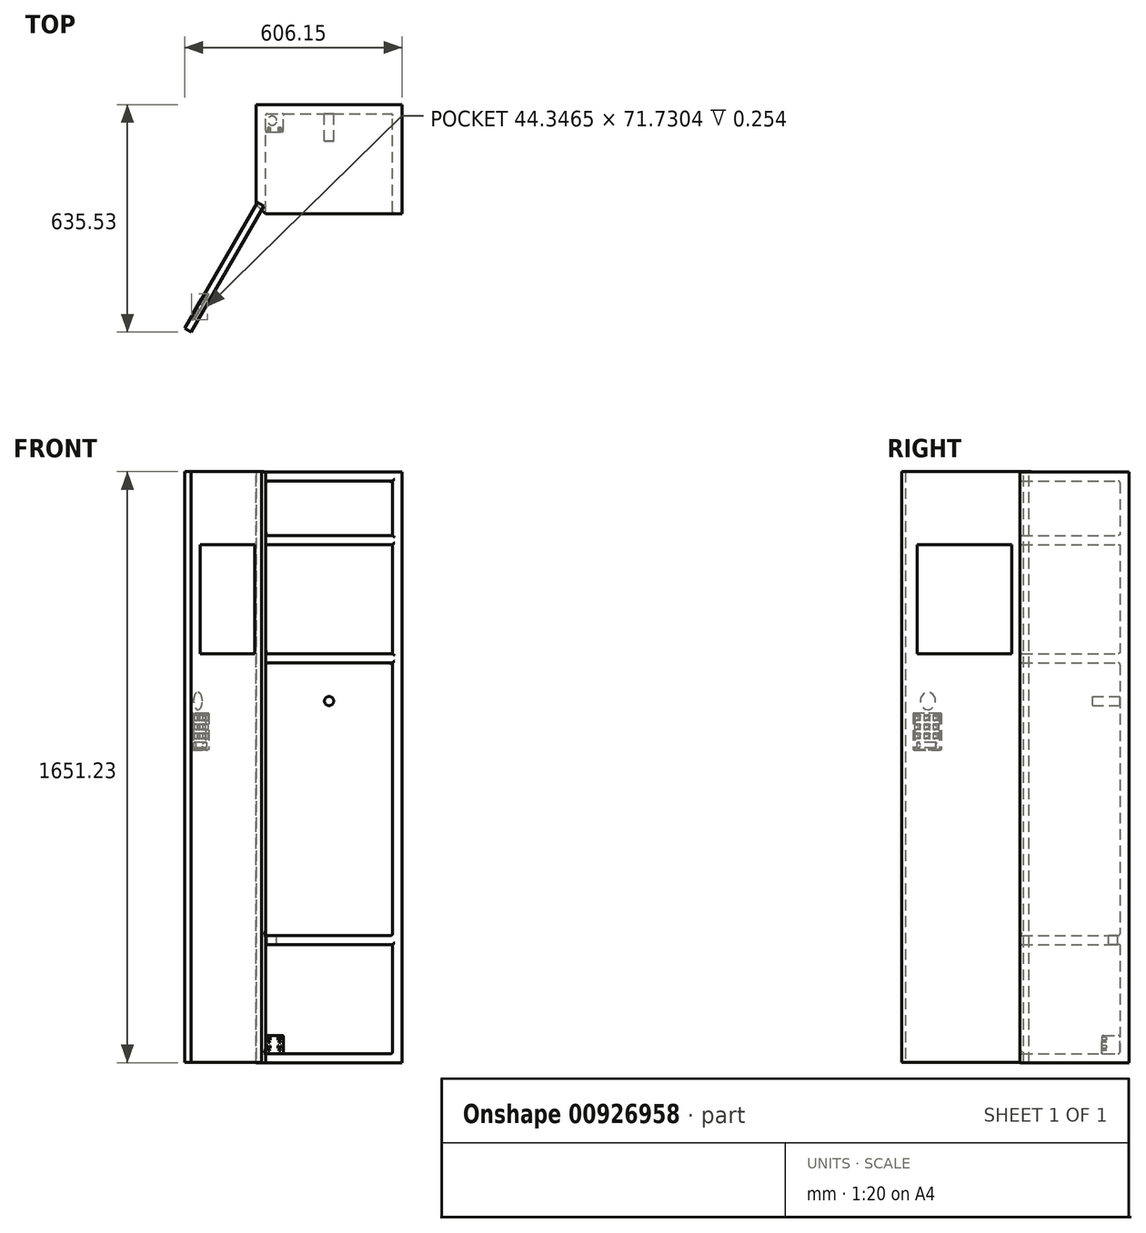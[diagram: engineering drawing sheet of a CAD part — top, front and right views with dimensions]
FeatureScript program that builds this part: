
annotation { "Feature Type Name" : "Feature", "Feature Type Description" : "" }
export const myFeature = defineFeature(function(context is Context, id is Id, definition is map)
    precondition{}
    {
        {
            var Q0;
            Q0=qCreatedBy(makeId("Front.planeOp"),FACE);
            var sketch = newSketch(context, id + "F0", { "sketchPlane" : qUnion([Q0])});
            skLineSegment(sketch, "E0.bottom", {"start": v(-230.27, 1365.34) * mm, "end": v(176.13, 1365.34) * mm});
            skLineSegment(sketch, "E0.top", {"start": v(-230.27, -285.66) * mm, "end": v(176.13, -285.66) * mm});
            skLineSegment(sketch, "E0.left", {"start": v(-230.27, 1365.34) * mm, "end": v(-230.27, -285.66) * mm});
            skLineSegment(sketch, "E0.right", {"start": v(176.13, 1365.34) * mm, "end": v(176.13, -285.66) * mm});
            skSolve(sketch);
        }
        {
            var Q0;
            Q0 = qSketchRegion(id + "F0", true);
            extrude(context, id + "F1", {"entities" : qUnion([Q0]), "depth" : 304.8 * mm, "offsetDistance" : 25.4 * mm});
        }
        {
            var Q0;
            Q0=makeQuery(id+"F1.opExtrude","CAP_FACE",FACE,{"disambiguationData":[OSD([sQuery(id+"F0.wireOp",EDGE,"E0.bottom"),sQuery(id+"F0.wireOp",EDGE,"E0.top"),sQuery(id+"F0.wireOp",EDGE,"E0.left"),sQuery(id+"F0.wireOp",EDGE,"E0.right")])],"isStart":false});
            shell(context, id + "F2", {"entities" : qUnion([Q0]), "thickness" : 25.4 * mm});
        }
        {
            var Q0;
            Q0=makeQuery(id+"F2.opShell","OFFSET_FACE",FACE,{"disambiguationData":[OSD([sQuery(id+"F0.wireOp",EDGE,"E0.bottom"),sQuery(id+"F0.wireOp",EDGE,"E0.top"),sQuery(id+"F0.wireOp",EDGE,"E0.left"),sQuery(id+"F0.wireOp",EDGE,"E0.right")])]});
            var sketch = newSketch(context, id + "F3", { "sketchPlane" : qUnion([Q0])});
            skLineSegment(sketch, "E1.bottom", {"start": v(-204.87, 1187.54) * mm, "end": v(150.73, 1187.54) * mm});
            skLineSegment(sketch, "E1.top", {"start": v(-204.87, 1162.14) * mm, "end": v(150.73, 1162.14) * mm});
            skLineSegment(sketch, "E1.left", {"start": v(-204.87, 1187.54) * mm, "end": v(-204.87, 1162.14) * mm});
            skLineSegment(sketch, "E1.right", {"start": v(150.73, 1187.54) * mm, "end": v(150.73, 1162.14) * mm});
            skSolve(sketch);
        }
        {
            var Q0;
            Q0 = qSketchRegion(id + "F3", true);
            extrude(context, id + "F4", {"entities" : qUnion([Q0]), "operationType" : NewBodyOperationType.ADD, "depth" : 279.4 * mm, "offsetDistance" : 25.4 * mm});
        }
        {
            var Q0;
            {var subQ0=sQuery(id+"F0.wireOp",EDGE,"E0.top");var subQ1=sQuery(id+"F0.wireOp",EDGE,"E0.left");var subQ2=sQuery(id+"F0.wireOp",EDGE,"E0.right");Q0=makeQuery(id+"F4.boolean.opBoolean","SPLIT",FACE,{"disambiguationData":[TD([makeQuery(id+"F2.opShell","OFFSET_FACE",FACE,{"disambiguationData":[OSD([subQ0])]})])],"derivedFrom":makeQuery(id+"F2.opShell","OFFSET_FACE",FACE,{"disambiguationData":[OSD([sQuery(id+"F0.wireOp",EDGE,"E0.bottom"),subQ0,subQ1,subQ2])]})});}
            var sketch = newSketch(context, id + "F5", { "sketchPlane" : qUnion([Q0])});
            skLineSegment(sketch, "E2.bottom", {"start": v(-204.87, 857.34) * mm, "end": v(150.73, 857.34) * mm});
            skLineSegment(sketch, "E2.top", {"start": v(-204.87, 831.94) * mm, "end": v(150.73, 831.94) * mm});
            skLineSegment(sketch, "E2.left", {"start": v(-204.87, 857.34) * mm, "end": v(-204.87, 831.94) * mm});
            skLineSegment(sketch, "E2.right", {"start": v(150.73, 857.34) * mm, "end": v(150.73, 831.94) * mm});
            skLineSegment(sketch, "E3.bottom", {"start": v(-204.87, 44.54) * mm, "end": v(150.73, 44.54) * mm});
            skLineSegment(sketch, "E3.top", {"start": v(-204.87, 69.94) * mm, "end": v(150.73, 69.94) * mm});
            skLineSegment(sketch, "E3.left", {"start": v(-204.87, 44.54) * mm, "end": v(-204.87, 69.94) * mm});
            skLineSegment(sketch, "E3.right", {"start": v(150.73, 44.54) * mm, "end": v(150.73, 69.94) * mm});
            skSolve(sketch);
        }
        {
            var Q0;
            Q0 = qSketchRegion(id + "F5", true);
            extrude(context, id + "F6", {"entities" : qUnion([Q0]), "operationType" : NewBodyOperationType.ADD, "depth" : 279.4 * mm, "offsetDistance" : 25.4 * mm});
        }
        {
            var Q0;
            Q0 = qSketchRegion(id + "F5", true);
            extrude(context, id + "F7", {"entities" : qUnion([Q0]), "operationType" : NewBodyOperationType.ADD, "depth" : 25.4 * mm, "offsetDistance" : 25.4 * mm});
        }
        {
            var Q0;
            {var subQ0=sQuery(id+"F0.wireOp",EDGE,"E0.left");var subQ2=sQuery(id+"F0.wireOp",EDGE,"E0.right");var subQ4=sQuery(id+"F0.wireOp",EDGE,"E0.top");Q0=makeQuery(id+"F6.boolean.opBoolean","SPLIT",FACE,{"disambiguationData":[TD([makeQuery(id+"F6.opExtrude","SWEPT_FACE",FACE,{"disambiguationData":[OSD([sQuery(id+"F5.wireOp",EDGE,"E2.top")])]})])],"derivedFrom":makeQuery(id+"F4.boolean.opBoolean","SPLIT",FACE,{"disambiguationData":[TD([makeQuery(id+"F2.opShell","OFFSET_FACE",FACE,{"disambiguationData":[OSD([subQ4])]})])],"derivedFrom":makeQuery(id+"F2.opShell","OFFSET_FACE",FACE,{"disambiguationData":[OSD([sQuery(id+"F0.wireOp",EDGE,"E0.bottom"),subQ4,subQ0,subQ2])]})})});}
            var sketch = newSketch(context, id + "F8", { "sketchPlane" : qUnion([Q0])});
            skCircle(sketch, "E4", {"center": v(-27.07, 724.69) * mm, "radius": 12.8 * mm});
            skPoint(sketch, "E4.centerSnap0", {"position": v(-27.07, 831.94) * mm});
            skSolve(sketch);
        }
        {
            var Q0;
            Q0 = qSketchRegion(id + "F8", true);
            extrude(context, id + "F9", {"entities" : qUnion([Q0]), "operationType" : NewBodyOperationType.ADD, "depth" : 76.2 * mm, "offsetDistance" : 25.4 * mm});
        }
        {
            var Q0;
            {var subQ0=sQuery(id+"F0.wireOp",EDGE,"E0.top");var subQ1=makeQuery(id+"F2.opShell","OFFSET_FACE",FACE,{"disambiguationData":[OSD([subQ0])]});var subQ2=sQuery(id+"F0.wireOp",EDGE,"E0.left");var subQ4=sQuery(id+"F0.wireOp",EDGE,"E0.right");Q0=makeQuery(id+"F6.boolean.opBoolean","SPLIT",FACE,{"disambiguationData":[TD([subQ1])],"derivedFrom":makeQuery(id+"F4.boolean.opBoolean","SPLIT",FACE,{"disambiguationData":[TD([subQ1])],"derivedFrom":makeQuery(id+"F2.opShell","OFFSET_FACE",FACE,{"disambiguationData":[OSD([sQuery(id+"F0.wireOp",EDGE,"E0.bottom"),subQ0,subQ2,subQ4])]})})});}
            var sketch = newSketch(context, id + "F10", { "sketchPlane" : qUnion([Q0])});
            skLineSegment(sketch, "E5.bottom", {"start": v(-204.87, -260.26) * mm, "end": v(-154.07, -260.26) * mm});
            skLineSegment(sketch, "E5.top", {"start": v(-204.87, -209.46) * mm, "end": v(-154.07, -209.46) * mm});
            skLineSegment(sketch, "E5.left", {"start": v(-204.87, -260.26) * mm, "end": v(-204.87, -209.46) * mm});
            skLineSegment(sketch, "E5.right", {"start": v(-154.07, -260.26) * mm, "end": v(-154.07, -209.46) * mm});
            skSolve(sketch);
        }
        {
            var Q0;
            Q0 = qSketchRegion(id + "F10", true);
            extrude(context, id + "F11", {"entities" : qUnion([Q0]), "operationType" : NewBodyOperationType.ADD, "depth" : 50.8 * mm, "offsetDistance" : 25.4 * mm});
        }
        {
            var Q0;
            {var subQ0=sQuery(id+"F3.wireOp",EDGE,"E1.top");var subQ2=sQuery(id+"F0.wireOp",EDGE,"E0.right");var subQ4=makeQuery(id+"F4.opExtrude","SWEPT_FACE",FACE,{"disambiguationData":[OSD([subQ0])]});var subQ5=sQuery(id+"F0.wireOp",EDGE,"E0.top");Q0=makeQuery(id+"F6.boolean.opBoolean","SPLIT",EDGE,{"disambiguationData":[TD([subQ4])],"derivedFrom":makeQuery(id+"F4.boolean.opBoolean","SPLIT",EDGE,{"disambiguationData":[TD([makeQuery(id+"F2.opShell","OFFSET_FACE",FACE,{"disambiguationData":[OSD([subQ5])]})])],"derivedFrom":makeQuery(id+"F2.opShell","OFFSET_EDGE",EDGE,{"disambiguationData":[OSD([subQ2]),TDD([makeQuery(id+"F1.opExtrude","CAP_EDGE",EDGE,{"disambiguationData":[OSD([subQ2])],"isStart":false})])]})})});}
            var Q1;
            {var subQ3=sQuery(id+"F5.wireOp",EDGE,"E2.top");var subQ4=sQuery(id+"F0.wireOp",EDGE,"E0.right");var subQ6=sQuery(id+"F0.wireOp",EDGE,"E0.top");Q1=makeQuery(id+"F6.boolean.opBoolean","SPLIT",EDGE,{"disambiguationData":[TD([makeQuery(id+"F6.opExtrude","SWEPT_FACE",FACE,{"disambiguationData":[OSD([subQ3])]})])],"derivedFrom":makeQuery(id+"F4.boolean.opBoolean","SPLIT",EDGE,{"disambiguationData":[TD([makeQuery(id+"F2.opShell","OFFSET_FACE",FACE,{"disambiguationData":[OSD([subQ6])]})])],"derivedFrom":makeQuery(id+"F2.opShell","OFFSET_EDGE",EDGE,{"disambiguationData":[OSD([subQ4]),TDD([makeQuery(id+"F1.opExtrude","CAP_EDGE",EDGE,{"disambiguationData":[OSD([subQ4])],"isStart":false})])]})})});}
            var Q2;
            {var subQ3=sQuery(id+"F0.wireOp",EDGE,"E0.right");var subQ5=sQuery(id+"F0.wireOp",EDGE,"E0.top");var subQ6=makeQuery(id+"F2.opShell","OFFSET_FACE",FACE,{"disambiguationData":[OSD([subQ5])]});Q2=makeQuery(id+"F6.boolean.opBoolean","SPLIT",EDGE,{"disambiguationData":[TD([subQ6])],"derivedFrom":makeQuery(id+"F4.boolean.opBoolean","SPLIT",EDGE,{"disambiguationData":[TD([subQ6])],"derivedFrom":makeQuery(id+"F2.opShell","OFFSET_EDGE",EDGE,{"disambiguationData":[OSD([subQ3]),TDD([makeQuery(id+"F1.opExtrude","CAP_EDGE",EDGE,{"disambiguationData":[OSD([subQ3])],"isStart":false})])]})})});}
            var Q3;
            {var subQ0=sQuery(id+"F0.wireOp",EDGE,"E0.top");Q3=makeQuery(id+"F2.opShell","OFFSET_EDGE",EDGE,{"disambiguationData":[OSD([subQ0]),TDD([makeQuery(id+"F1.opExtrude","CAP_EDGE",EDGE,{"disambiguationData":[OSD([subQ0])],"isStart":false})])]});}
            var Q4;
            Q4=makeQuery(id+"F6.opExtrude","CAP_EDGE",EDGE,{"disambiguationData":[OSD([sQuery(id+"F5.wireOp",EDGE,"E3.bottom")])],"isStart":false});
            var Q5;
            Q5=makeQuery(id+"F6.opExtrude","CAP_EDGE",EDGE,{"disambiguationData":[OSD([sQuery(id+"F5.wireOp",EDGE,"E3.top")])],"isStart":false});
            var Q6;
            Q6=makeQuery(id+"F6.opExtrude","CAP_EDGE",EDGE,{"disambiguationData":[OSD([sQuery(id+"F5.wireOp",EDGE,"E2.top")])],"isStart":false});
            var Q7;
            Q7=makeQuery(id+"F4.opExtrude","CAP_EDGE",EDGE,{"disambiguationData":[OSD([sQuery(id+"F3.wireOp",EDGE,"E1.top")])],"isStart":false});
            var Q8;
            Q8=makeQuery(id+"F6.opExtrude","CAP_EDGE",EDGE,{"disambiguationData":[OSD([sQuery(id+"F5.wireOp",EDGE,"E2.bottom")])],"isStart":true});
            var Q9;
            Q9=makeQuery(id+"F4.opExtrude","CAP_EDGE",EDGE,{"disambiguationData":[OSD([sQuery(id+"F3.wireOp",EDGE,"E1.bottom")])],"isStart":false});
            var Q10;
            {var subQ1=sQuery(id+"F0.wireOp",EDGE,"E0.right");var subQ2=sQuery(id+"F0.wireOp",EDGE,"E0.bottom");Q10=makeQuery(id+"F4.boolean.opBoolean","SPLIT",EDGE,{"disambiguationData":[TD([makeQuery(id+"F2.opShell","OFFSET_FACE",FACE,{"disambiguationData":[OSD([subQ2])]})])],"derivedFrom":makeQuery(id+"F2.opShell","OFFSET_EDGE",EDGE,{"disambiguationData":[OSD([subQ1]),TDD([makeQuery(id+"F1.opExtrude","CAP_EDGE",EDGE,{"disambiguationData":[OSD([subQ1])],"isStart":false})])]})});}
            var Q11;
            {var subQ0=sQuery(id+"F0.wireOp",EDGE,"E0.bottom");Q11=makeQuery(id+"F2.opShell","OFFSET_EDGE",EDGE,{"disambiguationData":[OSD([subQ0]),TDD([makeQuery(id+"F1.opExtrude","CAP_EDGE",EDGE,{"disambiguationData":[OSD([subQ0])],"isStart":false})])]});}
            var Q12;
            Q12=makeQuery(id+"F6.opExtrude","CAP_EDGE",EDGE,{"disambiguationData":[OSD([sQuery(id+"F5.wireOp",EDGE,"E2.bottom")])],"isStart":false});
            var Q13;
            Q13=makeQuery(id+"F6.opExtrude","CAP_EDGE",EDGE,{"disambiguationData":[OSD([sQuery(id+"F5.wireOp",EDGE,"E2.top")])],"isStart":true});
            var Q14;
            {var subQ0=sQuery(id+"F0.wireOp",EDGE,"E0.right");var subQ1=sQuery(id+"F0.wireOp",EDGE,"E0.top");Q14=makeQuery(id+"F6.boolean.opBoolean","SPLIT",EDGE,{"disambiguationData":[TD([makeQuery(id+"F6.opExtrude","SWEPT_FACE",FACE,{"disambiguationData":[OSD([sQuery(id+"F5.wireOp",EDGE,"E2.top")])]})])],"derivedFrom":makeQuery(id+"F4.boolean.opBoolean","SPLIT",EDGE,{"disambiguationData":[TD([makeQuery(id+"F2.opShell","OFFSET_FACE",FACE,{"disambiguationData":[OSD([subQ1])]})])],"derivedFrom":makeQuery(id+"F2.opShell","OFFSET_EDGE",EDGE,{"disambiguationData":[OSD([subQ0]),TDD([makeQuery(id+"F1.opExtrude","CAP_EDGE",EDGE,{"disambiguationData":[OSD([subQ0])],"isStart":true})])]})})});}
            var Q15;
            Q15=makeQuery(id+"F4.opExtrude","CAP_EDGE",EDGE,{"disambiguationData":[OSD([sQuery(id+"F3.wireOp",EDGE,"E1.bottom")])],"isStart":true});
            var Q16;
            {var subQ0=sQuery(id+"F0.wireOp",EDGE,"E0.bottom");var subQ1=sQuery(id+"F0.wireOp",EDGE,"E0.left");Q16=makeQuery(id+"F4.boolean.opBoolean","SPLIT",EDGE,{"disambiguationData":[TD([makeQuery(id+"F2.opShell","OFFSET_FACE",FACE,{"disambiguationData":[OSD([subQ0])]})])],"derivedFrom":makeQuery(id+"F2.opShell","OFFSET_EDGE",EDGE,{"disambiguationData":[OSD([subQ1]),TDD([makeQuery(id+"F1.opExtrude","CAP_EDGE",EDGE,{"disambiguationData":[OSD([subQ1])],"isStart":true})])]})});}
            var Q17;
            {var subQ0=sQuery(id+"F0.wireOp",EDGE,"E0.bottom");Q17=makeQuery(id+"F2.opShell","OFFSET_EDGE",EDGE,{"disambiguationData":[OSD([subQ0]),TDD([makeQuery(id+"F1.opExtrude","CAP_EDGE",EDGE,{"disambiguationData":[OSD([subQ0])],"isStart":true})])]});}
            var Q18;
            {var subQ0=sQuery(id+"F0.wireOp",EDGE,"E0.bottom");var subQ1=sQuery(id+"F0.wireOp",EDGE,"E0.right");Q18=makeQuery(id+"F4.boolean.opBoolean","SPLIT",EDGE,{"disambiguationData":[TD([makeQuery(id+"F2.opShell","OFFSET_FACE",FACE,{"disambiguationData":[OSD([subQ0])]})])],"derivedFrom":makeQuery(id+"F2.opShell","OFFSET_EDGE",EDGE,{"disambiguationData":[OSD([subQ1]),TDD([makeQuery(id+"F1.opExtrude","CAP_EDGE",EDGE,{"disambiguationData":[OSD([subQ1])],"isStart":true})])]})});}
            var Q19;
            Q19=makeQuery(id+"F4.opExtrude","CAP_EDGE",EDGE,{"disambiguationData":[OSD([sQuery(id+"F3.wireOp",EDGE,"E1.top")])],"isStart":true});
            var Q20;
            {var subQ0=sQuery(id+"F0.wireOp",EDGE,"E0.left");var subQ1=sQuery(id+"F0.wireOp",EDGE,"E0.top");var subQ3=makeQuery(id+"F4.opExtrude","SWEPT_FACE",FACE,{"disambiguationData":[OSD([sQuery(id+"F3.wireOp",EDGE,"E1.top")])]});Q20=makeQuery(id+"F6.boolean.opBoolean","SPLIT",EDGE,{"disambiguationData":[TD([subQ3])],"derivedFrom":makeQuery(id+"F4.boolean.opBoolean","SPLIT",EDGE,{"disambiguationData":[TD([makeQuery(id+"F2.opShell","OFFSET_FACE",FACE,{"disambiguationData":[OSD([subQ1])]})])],"derivedFrom":makeQuery(id+"F2.opShell","OFFSET_EDGE",EDGE,{"disambiguationData":[OSD([subQ0]),TDD([makeQuery(id+"F1.opExtrude","CAP_EDGE",EDGE,{"disambiguationData":[OSD([subQ0])],"isStart":true})])]})})});}
            var Q21;
            {var subQ0=sQuery(id+"F0.wireOp",EDGE,"E0.right");var subQ1=sQuery(id+"F0.wireOp",EDGE,"E0.top");var subQ3=makeQuery(id+"F4.opExtrude","SWEPT_FACE",FACE,{"disambiguationData":[OSD([sQuery(id+"F3.wireOp",EDGE,"E1.top")])]});Q21=makeQuery(id+"F6.boolean.opBoolean","SPLIT",EDGE,{"disambiguationData":[TD([subQ3])],"derivedFrom":makeQuery(id+"F4.boolean.opBoolean","SPLIT",EDGE,{"disambiguationData":[TD([makeQuery(id+"F2.opShell","OFFSET_FACE",FACE,{"disambiguationData":[OSD([subQ1])]})])],"derivedFrom":makeQuery(id+"F2.opShell","OFFSET_EDGE",EDGE,{"disambiguationData":[OSD([subQ0]),TDD([makeQuery(id+"F1.opExtrude","CAP_EDGE",EDGE,{"disambiguationData":[OSD([subQ0])],"isStart":true})])]})})});}
            var Q22;
            {var subQ0=sQuery(id+"F0.wireOp",EDGE,"E0.left");var subQ1=sQuery(id+"F0.wireOp",EDGE,"E0.top");Q22=makeQuery(id+"F6.boolean.opBoolean","SPLIT",EDGE,{"disambiguationData":[TD([makeQuery(id+"F6.opExtrude","SWEPT_FACE",FACE,{"disambiguationData":[OSD([sQuery(id+"F5.wireOp",EDGE,"E2.top")])]})])],"derivedFrom":makeQuery(id+"F4.boolean.opBoolean","SPLIT",EDGE,{"disambiguationData":[TD([makeQuery(id+"F2.opShell","OFFSET_FACE",FACE,{"disambiguationData":[OSD([subQ1])]})])],"derivedFrom":makeQuery(id+"F2.opShell","OFFSET_EDGE",EDGE,{"disambiguationData":[OSD([subQ0]),TDD([makeQuery(id+"F1.opExtrude","CAP_EDGE",EDGE,{"disambiguationData":[OSD([subQ0])],"isStart":true})])]})})});}
            var Q23;
            Q23=makeQuery(id+"F6.opExtrude","CAP_EDGE",EDGE,{"disambiguationData":[OSD([sQuery(id+"F5.wireOp",EDGE,"E3.top")])],"isStart":true});
            var Q24;
            Q24=makeQuery(id+"F6.opExtrude","SWEPT_EDGE",EDGE,{"disambiguationData":[OSD([sQuery(id+"F0.wireOp",EDGE,"E0.left"),sQuery(id+"F5.wireOp",EDGE,"E3.top"),sQuery(id+"F5.wireOp",EDGE,"E3.left")])]});
            var Q25;
            Q25=makeQuery(id+"F6.opExtrude","SWEPT_EDGE",EDGE,{"disambiguationData":[OSD([sQuery(id+"F0.wireOp",EDGE,"E0.right"),sQuery(id+"F5.wireOp",EDGE,"E3.top"),sQuery(id+"F5.wireOp",EDGE,"E3.right")])]});
            var Q26;
            Q26=makeQuery(id+"F2.opShell","OFFSET_EDGE",EDGE,{"disambiguationData":[OSD([sQuery(id+"F0.wireOp",EDGE,"E0.top"),sQuery(id+"F0.wireOp",EDGE,"E0.right")])]});
            var Q27;
            {var subQ0=sQuery(id+"F0.wireOp",EDGE,"E0.top");Q27=makeQuery(id+"F2.opShell","OFFSET_EDGE",EDGE,{"disambiguationData":[OSD([subQ0]),TDD([makeQuery(id+"F1.opExtrude","CAP_EDGE",EDGE,{"disambiguationData":[OSD([subQ0])],"isStart":true})])]});}
            var Q28;
            {var subQ0=sQuery(id+"F0.wireOp",EDGE,"E0.right");var subQ1=sQuery(id+"F0.wireOp",EDGE,"E0.top");var subQ3=makeQuery(id+"F2.opShell","OFFSET_FACE",FACE,{"disambiguationData":[OSD([subQ1])]});Q28=makeQuery(id+"F6.boolean.opBoolean","SPLIT",EDGE,{"disambiguationData":[TD([subQ3])],"derivedFrom":makeQuery(id+"F4.boolean.opBoolean","SPLIT",EDGE,{"disambiguationData":[TD([subQ3])],"derivedFrom":makeQuery(id+"F2.opShell","OFFSET_EDGE",EDGE,{"disambiguationData":[OSD([subQ0]),TDD([makeQuery(id+"F1.opExtrude","CAP_EDGE",EDGE,{"disambiguationData":[OSD([subQ0])],"isStart":true})])]})})});}
            var Q29;
            Q29=makeQuery(id+"F2.opShell","OFFSET_EDGE",EDGE,{"disambiguationData":[OSD([sQuery(id+"F0.wireOp",EDGE,"E0.top"),sQuery(id+"F0.wireOp",EDGE,"E0.left")])]});
            var Q30;
            {var subQ0=sQuery(id+"F0.wireOp",EDGE,"E0.left");var subQ1=sQuery(id+"F0.wireOp",EDGE,"E0.top");var subQ3=makeQuery(id+"F2.opShell","OFFSET_FACE",FACE,{"disambiguationData":[OSD([subQ1])]});Q30=makeQuery(id+"F6.boolean.opBoolean","SPLIT",EDGE,{"disambiguationData":[TD([subQ3])],"derivedFrom":makeQuery(id+"F4.boolean.opBoolean","SPLIT",EDGE,{"disambiguationData":[TD([subQ3])],"derivedFrom":makeQuery(id+"F2.opShell","OFFSET_EDGE",EDGE,{"disambiguationData":[OSD([subQ0]),TDD([makeQuery(id+"F1.opExtrude","CAP_EDGE",EDGE,{"disambiguationData":[OSD([subQ0])],"isStart":true})])]})})});}
            var Q31;
            Q31=makeQuery(id+"F11.opExtrude","CAP_EDGE",EDGE,{"disambiguationData":[OSD([sQuery(id+"F10.wireOp",EDGE,"E5.top")])],"isStart":false});
            var Q32;
            Q32=makeQuery(id+"F11.opExtrude","CAP_EDGE",EDGE,{"disambiguationData":[OSD([sQuery(id+"F10.wireOp",EDGE,"E5.bottom")])],"isStart":false});
            var Q33;
            Q33=makeQuery(id+"F11.opExtrude","SWEPT_EDGE",EDGE,{"disambiguationData":[OSD([sQuery(id+"F0.wireOp",EDGE,"E0.top"),sQuery(id+"F10.wireOp",EDGE,"E5.bottom"),sQuery(id+"F10.wireOp",EDGE,"E5.right")])]});
            var Q34;
            Q34=makeQuery(id+"F11.opExtrude","SWEPT_EDGE",EDGE,{"disambiguationData":[OSD([sQuery(id+"F10.wireOp",EDGE,"E5.top"),sQuery(id+"F10.wireOp",EDGE,"E5.right")])]});
            var Q35;
            Q35=makeQuery(id+"F11.opExtrude","CAP_EDGE",EDGE,{"disambiguationData":[OSD([sQuery(id+"F10.wireOp",EDGE,"E5.right")])],"isStart":false});
            fillet(context, id + "F12", {"entities" : qUnion([Q0, Q1, Q2, Q3, Q4, Q5, Q6, Q7, Q8, Q9, Q10, Q11, Q12, Q13, Q14, Q15, Q16, Q17, Q18, Q19, Q20, Q21, Q22, Q23, Q24, Q25, Q26, Q27, Q28, Q29, Q30, Q31, Q32, Q33, Q34, Q35]), "radius" : 5.08 * mm, "tangentPropagation" : true, "allowEdgeOverflow" : false});
        }
        {
            var Q0;
            Q0=makeQuery(id+"F11.opExtrude","CAP_FACE",FACE,{"disambiguationData":[OSD([sQuery(id+"F10.wireOp",EDGE,"E5.bottom"),sQuery(id+"F10.wireOp",EDGE,"E5.top"),sQuery(id+"F10.wireOp",EDGE,"E5.left"),sQuery(id+"F10.wireOp",EDGE,"E5.right")])],"isStart":false});
            var sketch = newSketch(context, id + "F13", { "sketchPlane" : qUnion([Q0])});
            skLineSegment(sketch, "E6.bottom", {"start": v(-162.97, -215.44) * mm, "end": v(-161.32, -215.44) * mm});
            skLineSegment(sketch, "E6.top", {"start": v(-162.97, -222.04) * mm, "end": v(-161.32, -222.04) * mm});
            skLineSegment(sketch, "E6.left", {"start": v(-162.97, -215.44) * mm, "end": v(-162.97, -222.04) * mm});
            skLineSegment(sketch, "E6.right", {"start": v(-161.32, -215.44) * mm, "end": v(-161.32, -222.04) * mm});
            skLineSegment(sketch, "E7.bottom", {"start": v(-169.6, -215.44) * mm, "end": v(-167.94, -215.44) * mm});
            skLineSegment(sketch, "E7.top", {"start": v(-169.6, -222.04) * mm, "end": v(-167.94, -222.04) * mm});
            skLineSegment(sketch, "E7.left", {"start": v(-169.6, -215.44) * mm, "end": v(-169.6, -222.04) * mm});
            skLineSegment(sketch, "E7.right", {"start": v(-167.94, -215.44) * mm, "end": v(-167.94, -222.04) * mm});
            skLineSegment(sketch, "E8", {"start": v(-167.76, -228.56) * mm, "end": v(-162.68, -228.56) * mm});
            skArc(sketch, "E9", {"start": v(-162.68, -228.56) * mm, "mid": v(-165.22, -226.02) * mm, "end": v(-167.76, -228.56) * mm});
            skLineSegment(sketch, "E10.bottom", {"start": v(-192.75, -215.64) * mm, "end": v(-191.1, -215.64) * mm});
            skLineSegment(sketch, "E10.top", {"start": v(-192.75, -222.24) * mm, "end": v(-191.1, -222.24) * mm});
            skLineSegment(sketch, "E10.left", {"start": v(-192.75, -215.64) * mm, "end": v(-192.75, -222.24) * mm});
            skLineSegment(sketch, "E10.right", {"start": v(-191.1, -215.64) * mm, "end": v(-191.1, -222.24) * mm});
            skLineSegment(sketch, "E11.bottom", {"start": v(-199.27, -215.64) * mm, "end": v(-197.61, -215.64) * mm});
            skLineSegment(sketch, "E11.top", {"start": v(-199.27, -222.24) * mm, "end": v(-197.61, -222.24) * mm});
            skLineSegment(sketch, "E11.left", {"start": v(-199.27, -215.64) * mm, "end": v(-199.27, -222.24) * mm});
            skLineSegment(sketch, "E11.right", {"start": v(-197.61, -215.64) * mm, "end": v(-197.61, -222.24) * mm});
            skLineSegment(sketch, "E12", {"start": v(-197.68, -228.56) * mm, "end": v(-192.6, -228.56) * mm});
            skArc(sketch, "E13", {"start": v(-192.6, -228.56) * mm, "mid": v(-195.14, -226.02) * mm, "end": v(-197.68, -228.56) * mm});
            skLineSegment(sketch, "E14.bottom", {"start": v(-162.9, -238.3) * mm, "end": v(-161.25, -238.3) * mm});
            skLineSegment(sketch, "E14.top", {"start": v(-162.9, -244.9) * mm, "end": v(-161.25, -244.9) * mm});
            skLineSegment(sketch, "E14.left", {"start": v(-162.9, -238.3) * mm, "end": v(-162.9, -244.9) * mm});
            skLineSegment(sketch, "E14.right", {"start": v(-161.25, -238.3) * mm, "end": v(-161.25, -244.9) * mm});
            skLineSegment(sketch, "E15.bottom", {"start": v(-169.53, -238.3) * mm, "end": v(-167.87, -238.3) * mm});
            skLineSegment(sketch, "E15.top", {"start": v(-169.53, -244.9) * mm, "end": v(-167.87, -244.9) * mm});
            skLineSegment(sketch, "E15.left", {"start": v(-169.53, -238.3) * mm, "end": v(-169.53, -244.9) * mm});
            skLineSegment(sketch, "E15.right", {"start": v(-167.87, -238.3) * mm, "end": v(-167.87, -244.9) * mm});
            skLineSegment(sketch, "E16", {"start": v(-167.7, -251.42) * mm, "end": v(-162.61, -251.42) * mm});
            skArc(sketch, "E17", {"start": v(-162.61, -251.42) * mm, "mid": v(-165.15, -248.88) * mm, "end": v(-167.7, -251.42) * mm});
            skLineSegment(sketch, "E18.bottom", {"start": v(-192.69, -238.5) * mm, "end": v(-191.03, -238.5) * mm});
            skLineSegment(sketch, "E18.top", {"start": v(-192.69, -245.1) * mm, "end": v(-191.03, -245.1) * mm});
            skLineSegment(sketch, "E18.left", {"start": v(-192.69, -238.5) * mm, "end": v(-192.69, -245.1) * mm});
            skLineSegment(sketch, "E18.right", {"start": v(-191.03, -238.5) * mm, "end": v(-191.03, -245.1) * mm});
            skLineSegment(sketch, "E19.bottom", {"start": v(-199.2, -238.5) * mm, "end": v(-197.55, -238.5) * mm});
            skLineSegment(sketch, "E19.top", {"start": v(-199.2, -245.1) * mm, "end": v(-197.55, -245.1) * mm});
            skLineSegment(sketch, "E19.left", {"start": v(-199.2, -238.5) * mm, "end": v(-199.2, -245.1) * mm});
            skLineSegment(sketch, "E19.right", {"start": v(-197.55, -238.5) * mm, "end": v(-197.55, -245.1) * mm});
            skLineSegment(sketch, "E20", {"start": v(-197.61, -251.42) * mm, "end": v(-192.53, -251.42) * mm});
            skArc(sketch, "E21", {"start": v(-192.53, -251.42) * mm, "mid": v(-195.07, -248.88) * mm, "end": v(-197.61, -251.42) * mm});
            skSolve(sketch);
        }
        {
            var Q0;
            Q0 = qSketchRegion(id + "F13", true);
            extrude(context, id + "F14", {"entities" : qUnion([Q0]), "operationType" : NewBodyOperationType.REMOVE, "oppositeDirection" : true, "depth" : 12.7 * mm, "offsetDistance" : 25.4 * mm});
        }
        {
            var Q0;
            Q0=makeQuery(id+"F6.opExtrude","SWEPT_FACE",FACE,{"disambiguationData":[OSD([sQuery(id+"F5.wireOp",EDGE,"E3.top")])]});
            var sketch = newSketch(context, id + "F15", { "sketchPlane" : qUnion([Q0])});
            skCircle(sketch, "E22", {"center": v(-185.89, -44.65) * mm, "radius": 12.7 * mm});
            skSolve(sketch);
        }
        {
            var Q0;
            Q0 = qSketchRegion(id + "F15", true);
            extrude(context, id + "F16", {"entities" : qUnion([Q0]), "operationType" : NewBodyOperationType.REMOVE, "oppositeDirection" : true, "depth" : 25.4 * mm, "offsetDistance" : 25.4 * mm});
        }
        {
            var Q0;
            Q0=makeQuery(id+"F1.opExtrude","CAP_EDGE",EDGE,{"disambiguationData":[OSD([sQuery(id+"F0.wireOp",EDGE,"E0.left")])],"isStart":false});
            chamfer(context, id + "F17", {"entities" : qUnion([Q0]), "width" : 25.4 * mm, "tangentPropagation" : true});
        }
        {
            var Q0;
            {var subQ0=sQuery(id+"F0.wireOp",EDGE,"E0.left");Q0=makeQuery(id+"F17.opChamfer","BLEND_EDGE",EDGE,{"blendedFrom":[makeQuery(id+"F1.opExtrude","CAP_EDGE",EDGE,{"disambiguationData":[OSD([subQ0])],"isStart":false}),makeQuery(id+"F1.opExtrude","SWEPT_FACE",FACE,{"disambiguationData":[OSD([subQ0])]})],"blendedInto":[makeQuery(id+"F1.opExtrude","SWEPT_FACE",FACE,{"disambiguationData":[OSD([subQ0])]})]});}
            cPlane(context, id + "F18", {"entities" : qUnion([Q0]), "cplaneType" : CPlaneType.LINE_ANGLE, "offset" : 25.4 * mm, "angle" : 30 * degree, "oppositeDirection" : true, "width" : 152.4 * mm, "height" : 152.4 * mm});
        }
        {
            var Q0;
            Q0=qCreatedBy(id+"F18.planeOp",FACE);
            var sketch = newSketch(context, id + "F19", { "sketchPlane" : qUnion([Q0])});
            skLineSegment(sketch, "E23.bottom", {"start": v(-350.2, 1365.57) * mm, "end": v(-756.6, 1365.57) * mm});
            skLineSegment(sketch, "E23.top", {"start": v(-350.2, -285.43) * mm, "end": v(-756.6, -285.43) * mm});
            skLineSegment(sketch, "E23.left", {"start": v(-350.2, 1365.57) * mm, "end": v(-350.2, -285.43) * mm});
            skLineSegment(sketch, "E23.right", {"start": v(-756.6, 1365.57) * mm, "end": v(-756.6, -285.43) * mm});
            skSolve(sketch);
        }
        {
            var Q0;
            Q0 = qSketchRegion(id + "F19", true);
            extrude(context, id + "F20", {"entities" : qUnion([Q0]), "operationType" : NewBodyOperationType.ADD, "depth" : 20.32 * mm, "offsetDistance" : 25.4 * mm});
        }
        {
            var Q0;
            Q0=makeQuery(id+"F20.opExtrude","CAP_FACE",FACE,{"disambiguationData":[OSD([sQuery(id+"F19.wireOp",EDGE,"E23.bottom"),sQuery(id+"F19.wireOp",EDGE,"E23.top"),sQuery(id+"F19.wireOp",EDGE,"E23.left"),sQuery(id+"F19.wireOp",EDGE,"E23.right")])],"isStart":true});
            var sketch = newSketch(context, id + "F21", { "sketchPlane" : qUnion([Q0])});
            skLineSegment(sketch, "E24.bottom", {"start": v(640.92, 690) * mm, "end": v(725.9, 690) * mm});
            skLineSegment(sketch, "E24.top", {"start": v(640.92, 588.4) * mm, "end": v(725.9, 588.4) * mm});
            skLineSegment(sketch, "E24.left", {"start": v(640.92, 690) * mm, "end": v(640.92, 588.4) * mm});
            skLineSegment(sketch, "E24.right", {"start": v(725.9, 690) * mm, "end": v(725.9, 588.4) * mm});
            skSolve(sketch);
        }
        {
            var Q0;
            Q0=makeQuery(id+"F20.opExtrude","CAP_FACE",FACE,{"disambiguationData":[OSD([sQuery(id+"F19.wireOp",EDGE,"E23.bottom"),sQuery(id+"F19.wireOp",EDGE,"E23.top"),sQuery(id+"F19.wireOp",EDGE,"E23.left"),sQuery(id+"F19.wireOp",EDGE,"E23.right")])],"isStart":false});
            var sketch = newSketch(context, id + "F22", { "sketchPlane" : qUnion([Q0])});
            skLineSegment(sketch, "E25.bottom", {"start": v(-705.8, 1161.83) * mm, "end": v(-401, 1161.83) * mm});
            skLineSegment(sketch, "E25.top", {"start": v(-705.8, 857.03) * mm, "end": v(-401, 857.03) * mm});
            skLineSegment(sketch, "E25.left", {"start": v(-705.8, 1161.83) * mm, "end": v(-705.8, 857.03) * mm});
            skLineSegment(sketch, "E25.right", {"start": v(-401, 1161.83) * mm, "end": v(-401, 857.03) * mm});
            skSolve(sketch);
        }
        {
            var Q0;
            Q0 = qSketchRegion(id + "F21", true);
            extrude(context, id + "F23", {"entities" : qUnion([Q0]), "operationType" : NewBodyOperationType.REMOVE, "oppositeDirection" : true, "depth" : 10.16 * mm, "offsetDistance" : 25.4 * mm});
        }
        {
            var Q0;
            Q0=makeQuery(id+"F23.boolean.opBoolean","COPY",FACE,{"derivedFrom":makeQuery(id+"F23.opExtrude","CAP_FACE",FACE,{"disambiguationData":[OSD([sQuery(id+"F21.wireOp",EDGE,"E24.bottom"),sQuery(id+"F21.wireOp",EDGE,"E24.top"),sQuery(id+"F21.wireOp",EDGE,"E24.left"),sQuery(id+"F21.wireOp",EDGE,"E24.right")])],"isStart":false})});
            var sketch = newSketch(context, id + "F24", { "sketchPlane" : qUnion([Q0])});
            skLineSegment(sketch, "E26.bottom", {"start": v(646, 685) * mm, "end": v(661.24, 685) * mm});
            skLineSegment(sketch, "E26.top", {"start": v(646, 669.76) * mm, "end": v(661.24, 669.76) * mm});
            skLineSegment(sketch, "E26.left", {"start": v(646, 685) * mm, "end": v(646, 669.76) * mm});
            skLineSegment(sketch, "E26.right", {"start": v(661.24, 685) * mm, "end": v(661.24, 669.76) * mm});
            skLineSegment(sketch, "E27.bottom", {"start": v(675.1, 685) * mm, "end": v(690.33, 685) * mm});
            skLineSegment(sketch, "E27.top", {"start": v(675.1, 669.76) * mm, "end": v(690.33, 669.76) * mm});
            skLineSegment(sketch, "E27.left", {"start": v(675.1, 685) * mm, "end": v(675.1, 669.76) * mm});
            skLineSegment(sketch, "E27.right", {"start": v(690.33, 685) * mm, "end": v(690.33, 669.76) * mm});
            skLineSegment(sketch, "E28.bottom", {"start": v(705.57, 685) * mm, "end": v(720.81, 685) * mm});
            skLineSegment(sketch, "E28.top", {"start": v(705.57, 669.76) * mm, "end": v(720.81, 669.76) * mm});
            skLineSegment(sketch, "E28.left", {"start": v(705.57, 685) * mm, "end": v(705.57, 669.76) * mm});
            skLineSegment(sketch, "E28.right", {"start": v(720.81, 685) * mm, "end": v(720.81, 669.76) * mm});
            skLineSegment(sketch, "E29.bottom", {"start": v(646, 659.6) * mm, "end": v(661.24, 659.6) * mm});
            skLineSegment(sketch, "E29.top", {"start": v(646, 644.36) * mm, "end": v(661.24, 644.36) * mm});
            skLineSegment(sketch, "E29.left", {"start": v(646, 659.6) * mm, "end": v(646, 644.36) * mm});
            skLineSegment(sketch, "E29.right", {"start": v(661.24, 659.6) * mm, "end": v(661.24, 644.36) * mm});
            skLineSegment(sketch, "E30.bottom", {"start": v(675.1, 659.6) * mm, "end": v(690.33, 659.6) * mm});
            skLineSegment(sketch, "E30.top", {"start": v(675.1, 644.36) * mm, "end": v(690.33, 644.36) * mm});
            skLineSegment(sketch, "E30.left", {"start": v(675.1, 659.6) * mm, "end": v(675.1, 644.36) * mm});
            skLineSegment(sketch, "E30.right", {"start": v(690.33, 659.6) * mm, "end": v(690.33, 644.36) * mm});
            skLineSegment(sketch, "E31.bottom", {"start": v(705.57, 659.6) * mm, "end": v(720.81, 659.6) * mm});
            skLineSegment(sketch, "E31.top", {"start": v(705.57, 644.36) * mm, "end": v(720.81, 644.36) * mm});
            skLineSegment(sketch, "E31.left", {"start": v(705.57, 659.6) * mm, "end": v(705.57, 644.36) * mm});
            skLineSegment(sketch, "E31.right", {"start": v(720.81, 659.6) * mm, "end": v(720.81, 644.36) * mm});
            skLineSegment(sketch, "E32.bottom", {"start": v(646, 634.2) * mm, "end": v(661.24, 634.2) * mm});
            skLineSegment(sketch, "E32.top", {"start": v(646, 618.96) * mm, "end": v(661.24, 618.96) * mm});
            skLineSegment(sketch, "E32.left", {"start": v(646, 634.2) * mm, "end": v(646, 618.96) * mm});
            skLineSegment(sketch, "E32.right", {"start": v(661.24, 634.2) * mm, "end": v(661.24, 618.96) * mm});
            skLineSegment(sketch, "E33.bottom", {"start": v(675.1, 634.2) * mm, "end": v(690.33, 634.2) * mm});
            skLineSegment(sketch, "E33.top", {"start": v(675.1, 618.96) * mm, "end": v(690.33, 618.96) * mm});
            skLineSegment(sketch, "E33.left", {"start": v(675.1, 634.2) * mm, "end": v(675.1, 618.96) * mm});
            skLineSegment(sketch, "E33.right", {"start": v(690.33, 634.2) * mm, "end": v(690.33, 618.96) * mm});
            skLineSegment(sketch, "E34.bottom", {"start": v(705.57, 634.2) * mm, "end": v(720.81, 634.2) * mm});
            skLineSegment(sketch, "E34.top", {"start": v(705.57, 618.96) * mm, "end": v(720.81, 618.96) * mm});
            skLineSegment(sketch, "E34.left", {"start": v(705.57, 634.2) * mm, "end": v(705.57, 618.96) * mm});
            skLineSegment(sketch, "E34.right", {"start": v(720.81, 634.2) * mm, "end": v(720.81, 618.96) * mm});
            skLineSegment(sketch, "E35.bottom", {"start": v(653.62, 608.8) * mm, "end": v(713.2, 608.8) * mm});
            skLineSegment(sketch, "E35.top", {"start": v(653.62, 593.56) * mm, "end": v(713.2, 593.56) * mm});
            skLineSegment(sketch, "E35.left", {"start": v(653.62, 608.8) * mm, "end": v(653.62, 593.56) * mm});
            skLineSegment(sketch, "E35.right", {"start": v(713.2, 608.8) * mm, "end": v(713.2, 593.56) * mm});
            skLineSegment(sketch, "E36", {"start": v(646, 669.76) * mm, "end": v(646, 659.6) * mm});
            skLineSegment(sketch, "E37", {"start": v(646, 644.36) * mm, "end": v(646, 634.2) * mm});
            skLineSegment(sketch, "E38", {"start": v(690.33, 669.76) * mm, "end": v(705.57, 669.76) * mm});
            skLineSegment(sketch, "E39", {"start": v(690.33, 644.36) * mm, "end": v(705.57, 644.36) * mm});
            skLineSegment(sketch, "E40", {"start": v(661.24, 618.96) * mm, "end": v(675.1, 618.96) * mm});
            skLineSegment(sketch, "E41", {"start": v(690.33, 618.96) * mm, "end": v(705.57, 618.96) * mm});
            skLineSegment(sketch, "E42", {"start": v(690.33, 669.76) * mm, "end": v(690.33, 659.6) * mm});
            skLineSegment(sketch, "E43", {"start": v(690.33, 644.36) * mm, "end": v(690.33, 634.2) * mm});
            skSolve(sketch);
        }
        {
            var Q0;
            Q0 = qSketchRegion(id + "F22", true);
            extrude(context, id + "F25", {"entities" : qUnion([Q0]), "operationType" : NewBodyOperationType.ADD, "depth" : 0.25 * mm, "offsetDistance" : 25.4 * mm});
        }
        {
            var Q0;
            Q0=makeQuery(id+"F23.boolean.opBoolean","COPY",FACE,{"derivedFrom":makeQuery(id+"F23.opExtrude","SWEPT_FACE",FACE,{"disambiguationData":[OSD([sQuery(id+"F21.wireOp",EDGE,"E24.top")])]})});
            var sketch = newSketch(context, id + "F26", { "sketchPlane" : qUnion([Q0])});
            skLineSegment(sketch, "E44", {"start": v(-366.85, -531.2) * mm, "end": v(-406.8, -600.39) * mm});
            skLineSegment(sketch, "E45", {"start": v(-406.8, -600.39) * mm, "end": v(-411.2, -597.85) * mm});
            skLineSegment(sketch, "E46", {"start": v(-411.2, -597.85) * mm, "end": v(-371.25, -528.66) * mm});
            skLineSegment(sketch, "E47", {"start": v(-371.25, -528.66) * mm, "end": v(-366.85, -531.2) * mm});
            skSolve(sketch);
        }
        {
            var Q0;
            Q0 = qSketchRegion(id + "F26", true);
            extrude(context, id + "F27", {"entities" : qUnion([Q0]), "operationType" : NewBodyOperationType.REMOVE, "oppositeDirection" : true, "depth" : 0.25 * mm, "offsetDistance" : 25.4 * mm});
        }
        {
            var Q0;
            Q0 = qSketchRegion(id + "F24", true);
            extrude(context, id + "F28", {"entities" : qUnion([Q0]), "operationType" : NewBodyOperationType.ADD, "depth" : 10.16 * mm, "offsetDistance" : 25.4 * mm});
        }
        {
            var Q0;
            Q0=makeQuery(id+"F28.opExtrude","CAP_EDGE",EDGE,{"disambiguationData":[OSD([sQuery(id+"F24.wireOp",EDGE,"E26.left")])],"isStart":false});
            var Q1;
            Q1=makeQuery(id+"F28.opExtrude","CAP_EDGE",EDGE,{"disambiguationData":[OSD([sQuery(id+"F24.wireOp",EDGE,"E26.bottom")])],"isStart":false});
            var Q2;
            Q2=makeQuery(id+"F28.opExtrude","CAP_EDGE",EDGE,{"disambiguationData":[OSD([sQuery(id+"F24.wireOp",EDGE,"E26.right")])],"isStart":false});
            var Q3;
            Q3=makeQuery(id+"F28.opExtrude","CAP_EDGE",EDGE,{"disambiguationData":[OSD([sQuery(id+"F24.wireOp",EDGE,"E26.top")])],"isStart":false});
            var Q4;
            Q4=makeQuery(id+"F28.opExtrude","CAP_EDGE",EDGE,{"disambiguationData":[OSD([sQuery(id+"F24.wireOp",EDGE,"E27.bottom")])],"isStart":false});
            var Q5;
            Q5=makeQuery(id+"F28.opExtrude","CAP_EDGE",EDGE,{"disambiguationData":[OSD([sQuery(id+"F24.wireOp",EDGE,"E27.top")])],"isStart":false});
            var Q6;
            Q6=makeQuery(id+"F28.opExtrude","CAP_EDGE",EDGE,{"disambiguationData":[OSD([sQuery(id+"F24.wireOp",EDGE,"E27.left")])],"isStart":false});
            var Q7;
            Q7=makeQuery(id+"F28.opExtrude","CAP_EDGE",EDGE,{"disambiguationData":[OSD([sQuery(id+"F24.wireOp",EDGE,"E27.right")])],"isStart":false});
            var Q8;
            Q8=makeQuery(id+"F28.opExtrude","CAP_EDGE",EDGE,{"disambiguationData":[OSD([sQuery(id+"F24.wireOp",EDGE,"E28.bottom")])],"isStart":false});
            var Q9;
            Q9=makeQuery(id+"F28.opExtrude","CAP_EDGE",EDGE,{"disambiguationData":[OSD([sQuery(id+"F24.wireOp",EDGE,"E28.left")])],"isStart":false});
            var Q10;
            Q10=makeQuery(id+"F28.opExtrude","CAP_EDGE",EDGE,{"disambiguationData":[OSD([sQuery(id+"F24.wireOp",EDGE,"E28.top")])],"isStart":false});
            var Q11;
            Q11=makeQuery(id+"F28.opExtrude","CAP_EDGE",EDGE,{"disambiguationData":[OSD([sQuery(id+"F24.wireOp",EDGE,"E28.right")])],"isStart":false});
            var Q12;
            Q12=makeQuery(id+"F28.opExtrude","CAP_EDGE",EDGE,{"disambiguationData":[OSD([sQuery(id+"F24.wireOp",EDGE,"E31.bottom")])],"isStart":false});
            var Q13;
            Q13=makeQuery(id+"F28.opExtrude","CAP_EDGE",EDGE,{"disambiguationData":[OSD([sQuery(id+"F24.wireOp",EDGE,"E31.top")])],"isStart":false});
            var Q14;
            Q14=makeQuery(id+"F28.opExtrude","CAP_EDGE",EDGE,{"disambiguationData":[OSD([sQuery(id+"F24.wireOp",EDGE,"E31.left")])],"isStart":false});
            var Q15;
            Q15=makeQuery(id+"F28.opExtrude","CAP_EDGE",EDGE,{"disambiguationData":[OSD([sQuery(id+"F24.wireOp",EDGE,"E31.right")])],"isStart":false});
            var Q16;
            Q16=makeQuery(id+"F28.opExtrude","CAP_EDGE",EDGE,{"disambiguationData":[OSD([sQuery(id+"F24.wireOp",EDGE,"E30.right")])],"isStart":false});
            var Q17;
            Q17=makeQuery(id+"F28.opExtrude","CAP_EDGE",EDGE,{"disambiguationData":[OSD([sQuery(id+"F24.wireOp",EDGE,"E29.right")])],"isStart":false});
            var Q18;
            Q18=makeQuery(id+"F28.opExtrude","CAP_EDGE",EDGE,{"disambiguationData":[OSD([sQuery(id+"F24.wireOp",EDGE,"E32.right")])],"isStart":false});
            var Q19;
            Q19=makeQuery(id+"F28.opExtrude","CAP_EDGE",EDGE,{"disambiguationData":[OSD([sQuery(id+"F24.wireOp",EDGE,"E33.right")])],"isStart":false});
            var Q20;
            Q20=makeQuery(id+"F28.opExtrude","CAP_EDGE",EDGE,{"disambiguationData":[OSD([sQuery(id+"F24.wireOp",EDGE,"E34.right")])],"isStart":false});
            var Q21;
            Q21=makeQuery(id+"F28.opExtrude","CAP_EDGE",EDGE,{"disambiguationData":[OSD([sQuery(id+"F24.wireOp",EDGE,"E34.bottom")])],"isStart":false});
            var Q22;
            Q22=makeQuery(id+"F28.opExtrude","CAP_EDGE",EDGE,{"disambiguationData":[OSD([sQuery(id+"F24.wireOp",EDGE,"E33.bottom")])],"isStart":false});
            var Q23;
            Q23=makeQuery(id+"F28.opExtrude","CAP_EDGE",EDGE,{"disambiguationData":[OSD([sQuery(id+"F24.wireOp",EDGE,"E32.bottom")])],"isStart":false});
            var Q24;
            Q24=makeQuery(id+"F28.opExtrude","CAP_EDGE",EDGE,{"disambiguationData":[OSD([sQuery(id+"F24.wireOp",EDGE,"E29.bottom")])],"isStart":false});
            var Q25;
            Q25=makeQuery(id+"F28.opExtrude","CAP_EDGE",EDGE,{"disambiguationData":[OSD([sQuery(id+"F24.wireOp",EDGE,"E30.bottom")])],"isStart":false});
            var Q26;
            Q26=makeQuery(id+"F28.opExtrude","CAP_EDGE",EDGE,{"disambiguationData":[OSD([sQuery(id+"F24.wireOp",EDGE,"E30.left")])],"isStart":false});
            var Q27;
            Q27=makeQuery(id+"F28.opExtrude","CAP_FACE",FACE,{"disambiguationData":[OSD([sQuery(id+"F24.wireOp",EDGE,"E29.bottom"),sQuery(id+"F24.wireOp",EDGE,"E29.top"),sQuery(id+"F24.wireOp",EDGE,"E29.left"),sQuery(id+"F24.wireOp",EDGE,"E29.right")])],"isStart":false});
            var Q28;
            Q28=makeQuery(id+"F28.opExtrude","CAP_EDGE",EDGE,{"disambiguationData":[OSD([sQuery(id+"F24.wireOp",EDGE,"E32.left")])],"isStart":false});
            var Q29;
            Q29=makeQuery(id+"F28.opExtrude","CAP_EDGE",EDGE,{"disambiguationData":[OSD([sQuery(id+"F24.wireOp",EDGE,"E33.left")])],"isStart":false});
            var Q30;
            Q30=makeQuery(id+"F28.opExtrude","CAP_EDGE",EDGE,{"disambiguationData":[OSD([sQuery(id+"F24.wireOp",EDGE,"E34.left")])],"isStart":false});
            var Q31;
            Q31=makeQuery(id+"F28.opExtrude","CAP_EDGE",EDGE,{"disambiguationData":[OSD([sQuery(id+"F24.wireOp",EDGE,"E34.top")])],"isStart":false});
            var Q32;
            Q32=makeQuery(id+"F28.opExtrude","CAP_EDGE",EDGE,{"disambiguationData":[OSD([sQuery(id+"F24.wireOp",EDGE,"E33.top")])],"isStart":false});
            var Q33;
            Q33=makeQuery(id+"F28.opExtrude","CAP_EDGE",EDGE,{"disambiguationData":[OSD([sQuery(id+"F24.wireOp",EDGE,"E32.top")])],"isStart":false});
            var Q34;
            Q34=makeQuery(id+"F28.opExtrude","CAP_EDGE",EDGE,{"disambiguationData":[OSD([sQuery(id+"F24.wireOp",EDGE,"E30.top")])],"isStart":false});
            var Q35;
            Q35=makeQuery(id+"F28.opExtrude","CAP_EDGE",EDGE,{"disambiguationData":[OSD([sQuery(id+"F24.wireOp",EDGE,"E35.bottom")])],"isStart":false});
            var Q36;
            Q36=makeQuery(id+"F28.opExtrude","CAP_EDGE",EDGE,{"disambiguationData":[OSD([sQuery(id+"F24.wireOp",EDGE,"E35.top")])],"isStart":false});
            var Q37;
            Q37=makeQuery(id+"F28.opExtrude","CAP_EDGE",EDGE,{"disambiguationData":[OSD([sQuery(id+"F24.wireOp",EDGE,"E35.left")])],"isStart":false});
            var Q38;
            Q38=makeQuery(id+"F28.opExtrude","CAP_EDGE",EDGE,{"disambiguationData":[OSD([sQuery(id+"F24.wireOp",EDGE,"E35.right")])],"isStart":false});
            fillet(context, id + "F29", {"entities" : qUnion([Q0, Q1, Q2, Q3, Q4, Q5, Q6, Q7, Q8, Q9, Q10, Q11, Q12, Q13, Q14, Q15, Q16, Q17, Q18, Q19, Q20, Q21, Q22, Q23, Q24, Q25, Q26, Q27, Q28, Q29, Q30, Q31, Q32, Q33, Q34, Q35, Q36, Q37, Q38]), "radius" : 5.08 * mm, "tangentPropagation" : true, "allowEdgeOverflow" : false});
        }
        {
            var Q0;
            Q0=makeQuery(id+"F20.opExtrude","CAP_FACE",FACE,{"disambiguationData":[OSD([sQuery(id+"F19.wireOp",EDGE,"E23.bottom"),sQuery(id+"F19.wireOp",EDGE,"E23.top"),sQuery(id+"F19.wireOp",EDGE,"E23.left"),sQuery(id+"F19.wireOp",EDGE,"E23.right")])],"isStart":true});
            var sketch = newSketch(context, id + "F30", { "sketchPlane" : qUnion([Q0])});
            skCircle(sketch, "E48", {"center": v(683.4, 725.07) * mm, "radius": 24.36 * mm});
            skPoint(sketch, "E48.centerSnap0", {"position": v(683.4, 690) * mm});
            skSolve(sketch);
        }
        {
            var Q0;
            Q0 = qSketchRegion(id + "F30", true);
            extrude(context, id + "F31", {"entities" : qUnion([Q0]), "operationType" : NewBodyOperationType.ADD, "depth" : 2.54 * mm, "offsetDistance" : 25.4 * mm});
        }
        {
            var Q0;
            Q0=makeQuery(id+"F31.opExtrude","CAP_EDGE",EDGE,{"disambiguationData":[OSD([sQuery(id+"F30.wireOp",EDGE,"E48")])],"isStart":false});
            fillet(context, id + "F32", {"entities" : qUnion([Q0]), "radius" : 5.08 * mm, "tangentPropagation" : true, "allowEdgeOverflow" : false});
        }
    });
